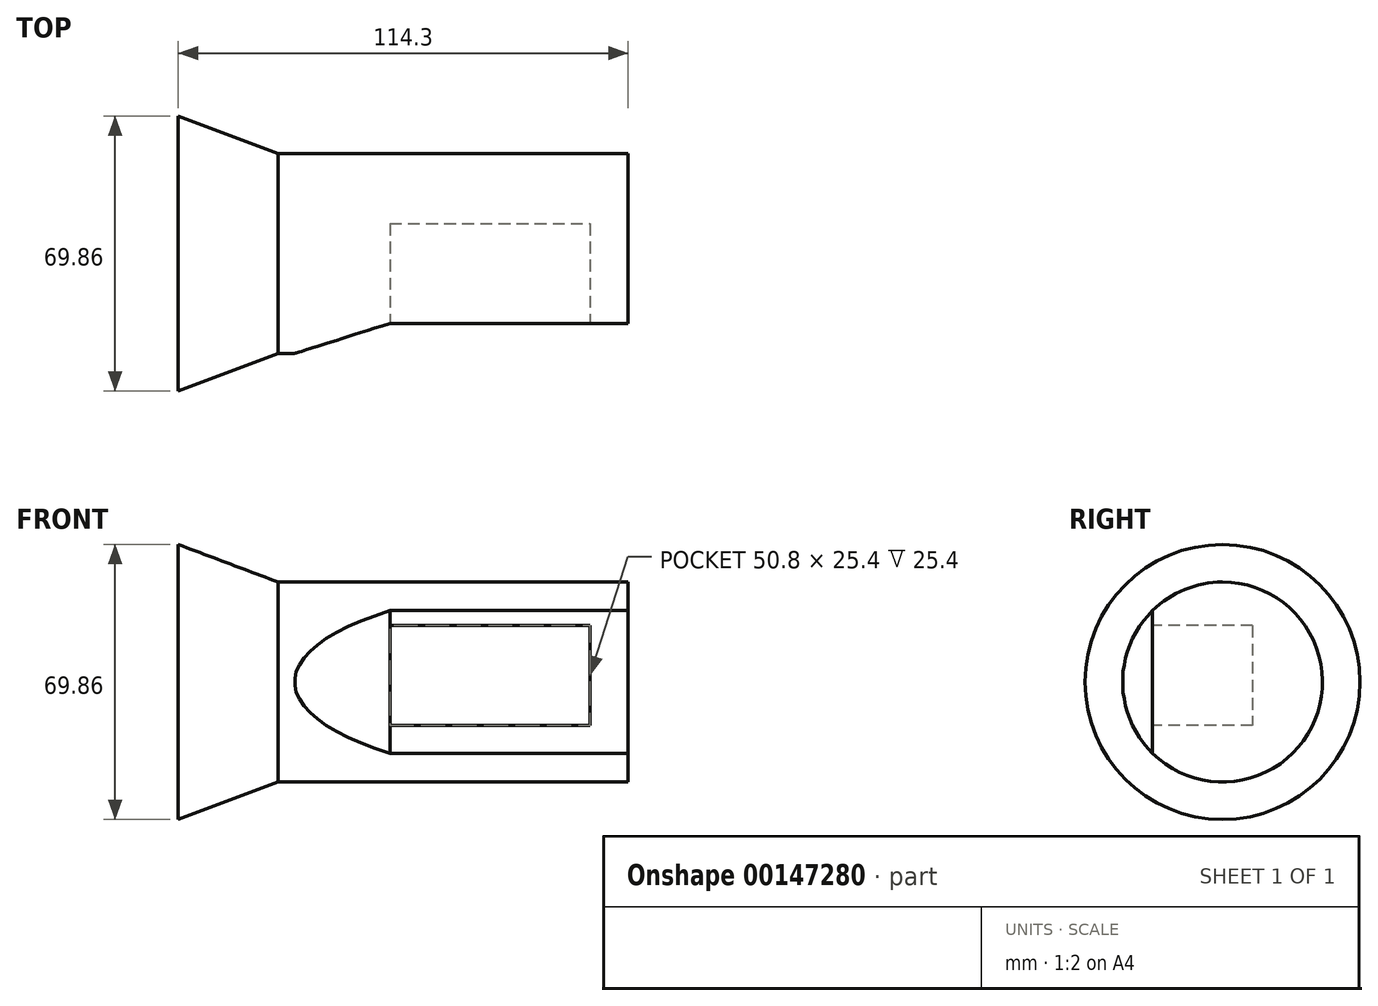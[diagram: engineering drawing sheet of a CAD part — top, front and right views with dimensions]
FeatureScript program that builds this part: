
annotation { "Feature Type Name" : "Feature", "Feature Type Description" : "" }
export const myFeature = defineFeature(function(context is Context, id is Id, definition is map)
    precondition{}
    {
        {
            var Q0;
            Q0=qCreatedBy(makeId("Front.planeOp"),FACE);
            var sketch = newSketch(context, id + "F0", { "sketchPlane" : qUnion([Q0])});
            skLineSegment(sketch, "E0", {"start": v(0, 25.4) * mm, "end": v(-32.08, 25.4) * mm});
            skLineSegment(sketch, "E1", {"start": v(0, 25.4) * mm, "end": v(56.82, 25.4) * mm});
            skLineSegment(sketch, "E2", {"start": v(56.82, 25.4) * mm, "end": v(56.82, 0) * mm});
            skLineSegment(sketch, "E3", {"start": v(-57.48, 0) * mm, "end": v(56.82, 0) * mm});
            skLineSegment(sketch, "E4", {"start": v(-57.48, 0) * mm, "end": v(-57.48, 34.92) * mm});
            skLineSegment(sketch, "E5", {"start": v(-57.48, 34.92) * mm, "end": v(-32.08, 25.4) * mm});
            skSolve(sketch);
        }
        {
            var Q0;
            Q0=qCreatedBy(makeId("Front.planeOp"),FACE);
            var sketch = newSketch(context, id + "F1", { "sketchPlane" : qUnion([Q0])});
            skLineSegment(sketch, "E6", {"start": v(-57.9, 0) * mm, "end": v(56.7, 0) * mm, "construction": true});
            skSolve(sketch);
        }
        {
            var Q0;
            Q0=makeQuery(id+"F0.imprint","IMPRINT",FACE,{"disambiguationData":[TD([[makeQuery(id+"F0.imprint","IMPRINT",EDGE,{"derivedFrom":sQuery(id+"F0.wireOp",EDGE,"E0")}),1.0]])]});
            var Q1;
            Q1=sQuery(id+"F0.wireOp",EDGE,"E3");
            revolve(context, id + "F2", {"entities" : qUnion([Q0]), "axis" : qUnion([Q1]), "revolveType" : RevolveType.FULL});
        }
        {
            var Q0;
            Q0=qCreatedBy(makeId("Top.planeOp"),FACE);
            var sketch = newSketch(context, id + "F3", { "sketchPlane" : qUnion([Q0])});
            skLineSegment(sketch, "E7", {"start": v(0, 0) * mm, "end": v(-32.05, -25.62) * mm});
            skSolve(sketch);
        }
        {
            var Q0;
            Q0=qCreatedBy(makeId("Top.planeOp"),FACE);
            var sketch = newSketch(context, id + "F4", { "sketchPlane" : qUnion([Q0])});
            skLineSegment(sketch, "E8", {"start": v(58.42, -30.92) * mm, "end": v(58.42, -17.78) * mm});
            skLineSegment(sketch, "E9", {"start": v(58.42, -17.78) * mm, "end": v(-3.7, -17.78) * mm});
            skLineSegment(sketch, "E10", {"start": v(-3.7, -17.78) * mm, "end": v(-27.94, -25.4) * mm});
            skLineSegment(sketch, "E11", {"start": v(-27.94, -25.4) * mm, "end": v(-27.94, -30.92) * mm});
            skLineSegment(sketch, "E12", {"start": v(-27.94, -30.92) * mm, "end": v(58.42, -30.92) * mm});
            skSolve(sketch);
        }
        {
            var Q0;
            Q0=makeQuery(id+"F4.imprint","IMPRINT",FACE,{"disambiguationData":[TD([[makeQuery(id+"F4.imprint","IMPRINT",EDGE,{"derivedFrom":sQuery(id+"F4.wireOp",EDGE,"E8")}),1.0]])]});
            extrude(context, id + "F5", {"entities" : qUnion([Q0]), "operationType" : NewBodyOperationType.REMOVE, "endBound" : BoundingType.SYMMETRIC, "oppositeDirection" : true, "depth" : 50.8 * mm});
        }
        {
            var Q0;
            Q0=makeQuery(id+"F5.boolean.opBoolean","COPY",FACE,{"derivedFrom":makeQuery(id+"F5.opExtrude","SWEPT_FACE",FACE,{"disambiguationData":[OSD([sQuery(id+"F4.wireOp",EDGE,"E9")])]})});
            cPlane(context, id + "F6", {"entities" : qUnion([Q0]), "cplaneType" : CPlaneType.OFFSET, "offset" : 25.4 * mm, "width" : 152.4 * mm, "height" : 152.4 * mm});
        }
        {
            var Q0;
            Q0=qCreatedBy(id+"F6.planeOp",FACE);
            var sketch = newSketch(context, id + "F7", { "sketchPlane" : qUnion([Q0])});
            skLineSegment(sketch, "E13.bottom", {"start": v(-3.7, 14.33) * mm, "end": v(47.1, 14.33) * mm});
            skLineSegment(sketch, "E13.top", {"start": v(-3.7, -11.07) * mm, "end": v(47.1, -11.07) * mm});
            skLineSegment(sketch, "E13.left", {"start": v(-3.7, 14.33) * mm, "end": v(-3.7, -11.07) * mm});
            skLineSegment(sketch, "E13.right", {"start": v(47.1, 14.33) * mm, "end": v(47.1, -11.07) * mm});
            skSolve(sketch);
        }
        {
            var Q0;
            Q0=makeQuery(id+"F7.imprint","IMPRINT",FACE,{"disambiguationData":[TD([[makeQuery(id+"F7.imprint","IMPRINT",EDGE,{"derivedFrom":sQuery(id+"F7.wireOp",EDGE,"E13.bottom")}),-1.0]])]});
            extrude(context, id + "F8", {"entities" : qUnion([Q0]), "operationType" : NewBodyOperationType.REMOVE, "oppositeDirection" : true, "depth" : 50.8 * mm});
        }
        {
            var Q0;
            Q0=makeQuery(id+"F2.opRevolve","SWEPT_FACE",FACE,{"disambiguationData":[OSD([sQuery(id+"F0.wireOp",EDGE,"E2")])]});
            cPlane(context, id + "F9", {"entities" : qUnion([Q0]), "cplaneType" : CPlaneType.OFFSET, "offset" : 6.35 * mm, "width" : 152.4 * mm, "height" : 152.4 * mm});
        }
        {
            var Q0;
            Q0=qCreatedBy(id+"F9.planeOp",FACE);
            var sketch = newSketch(context, id + "F10", { "sketchPlane" : qUnion([Q0])});
            skArc(sketch, "E14", {"start": v(0, -25.56) * mm, "mid": v(12.72, -0.13) * mm, "end": v(0, 25.3) * mm});
            skLineSegment(sketch, "E15", {"start": v(0, 25.3) * mm, "end": v(0, -25.56) * mm, "construction": true});
            skSolve(sketch);
        }
    });
